# Revit family: BISLEY_AOC_Filing_Cabinets
name_source: partatom
category: Furniture
revit_build: Autodesk Revit 2018 (Build: 20180423_1000(x64)
units: mm (PartAtom-declared; Revit-internal decimal feet)

## family parameters
Always vertical = Yes
Cut with Voids When Loaded = No
OmniClass Number = 23.40.20.00
OmniClass Title = General Furniture and Specialties
Room Calculation Point = No
Shared = No
Work Plane-Based = No

## types (3) — shared parameters
1623-1643 Visibility = Yes
1653 Visibility = No
Category = Furniture
Compliance Standards Certification = BS EN 14074 2004 Part 2 & 3
Depth = 622 mm  [stored 2.04068 ft]
Drawer width1 = 213 mm  [stored 0.698819 ft]
Drawer width2 = -213 mm  [stored -0.698819 ft]
Finish = Powder Coated
Label position = 135 mm
Label right = Yes
Lebel left = No
Manufacturer = Bisley
Material = Steel
Range = Filing Cabinets
Routine Maintenance = We recommend you clean your unit with warm water and a mild detergent solution. A damp cloth can be used to remove dust particles.
URL = www.bisley.com
Uniclass 2015 Code = PR_40_30_29
Uniclass2015Title = Shelves and Storage Units
Uniclass2015Version = V1.1
Warranty = 5 Years from date of purchase
Width = 470 mm  [stored 1.54199 ft]
plinth height = 70 mm  [stored 0.229659 ft]

## per-type parameters (varying)
| type | 3rd label vis | 4th label vis | Description | Dimensions | Height | Number of drawers | Product Information | Weight |
| AOC2 | No | No | 2 Drawer Cabinet | 711 x 470 x 622 mm | 711 mm | 2 | 2 Drawer Cabinet | 24.48 |
| AOC3 | Yes | No | 3 Drawer Cabinet | 1016 x 470 x 622 mm | 1016 mm | 3 | 3 Drawer Cabinet | 33.45kg |
| AOC4 | Yes | Yes | 4 Drawer Cabinet | 1321 x 470 x 622 mm | 1321 mm  [stored 4.33399 ft] | 4 | 4 Drawer Cabinet | 42.21kg |

note: column(s) folded — value = type name in every type: Model Reference, Name

note: [stored X ft] marks values corroborated as IEEE doubles in the binary element streams (Revit-internal decimal feet)

## geometry (parser evidence)
native form markers: Sweep x2
no freeform markers — native parametric forms only
